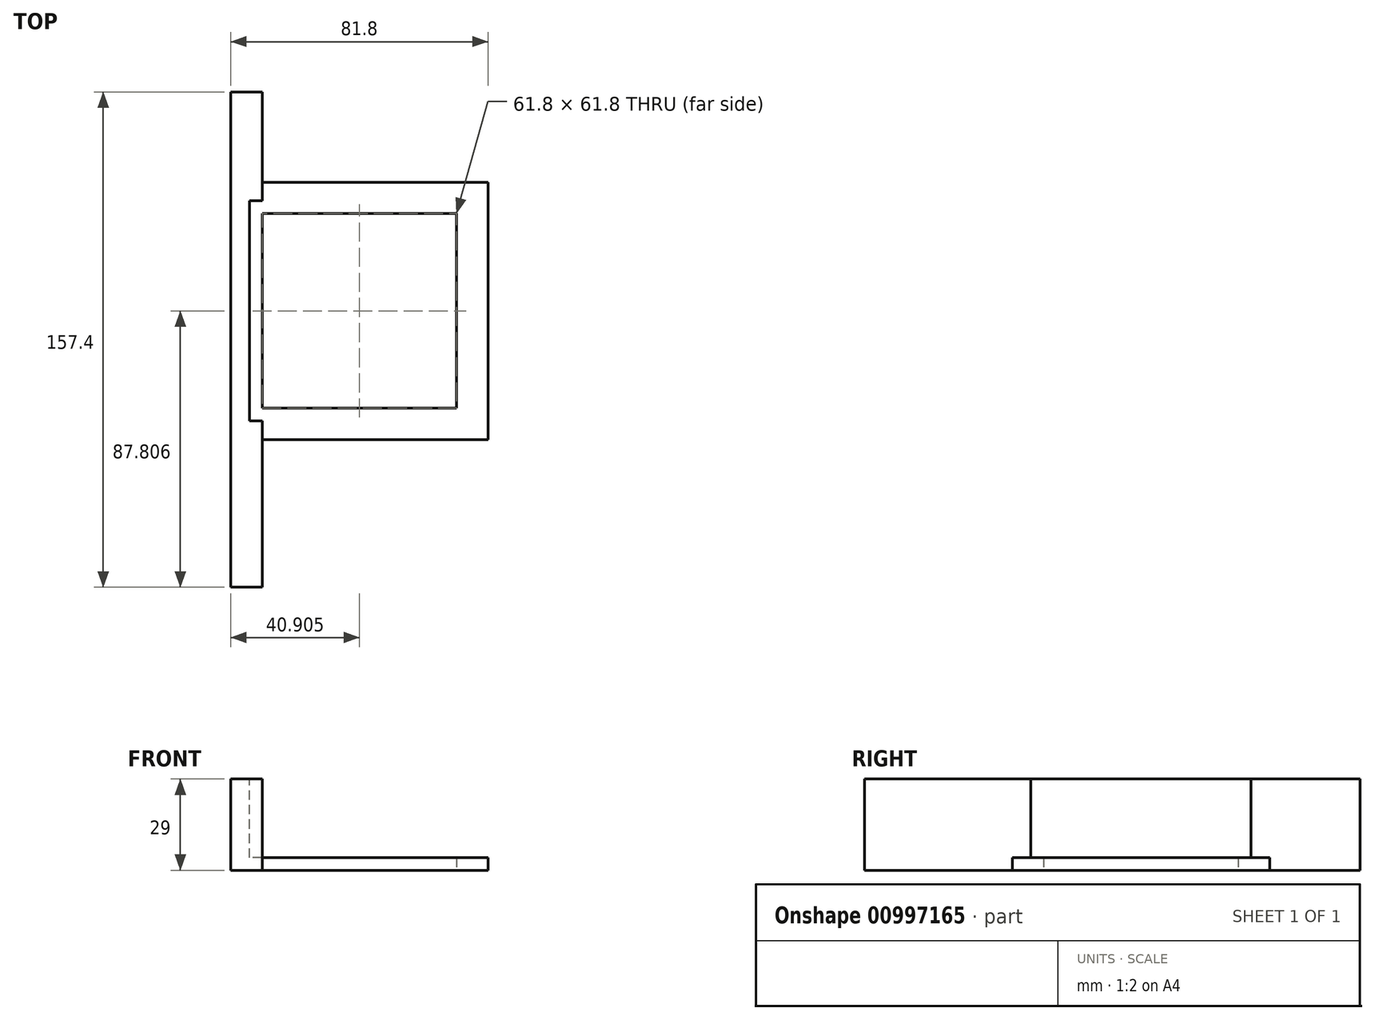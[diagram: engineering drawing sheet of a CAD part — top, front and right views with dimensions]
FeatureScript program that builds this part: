
annotation { "Feature Type Name" : "Feature", "Feature Type Description" : "" }
export const myFeature = defineFeature(function(context is Context, id is Id, definition is map)
    precondition{}
    {
        {
            var Q0;
            Q0=qCreatedBy(makeId("Top.planeOp"),FACE);
            var sketch = newSketch(context, id + "F0", { "sketchPlane" : qUnion([Q0])});
            skLineSegment(sketch, "E0.bottom", {"start": v(-15.62, 8.79) * mm, "end": v(35.18, 8.79) * mm, "construction": true});
            skLineSegment(sketch, "E0.top", {"start": v(-15.62, -42.01) * mm, "end": v(35.18, -42.01) * mm, "construction": true});
            skLineSegment(sketch, "E0.left", {"start": v(-15.62, 8.79) * mm, "end": v(-15.62, -42.01) * mm, "construction": true});
            skLineSegment(sketch, "E0.right", {"start": v(35.18, 8.79) * mm, "end": v(35.18, -42.01) * mm, "construction": true});
            skLineSegment(sketch, "E1", {"start": v(-2.92, 8.79) * mm, "end": v(-2.92, -3.91) * mm, "construction": true});
            skLineSegment(sketch, "E2", {"start": v(22.48, 8.79) * mm, "end": v(22.48, -3.91) * mm, "construction": true});
            skLineSegment(sketch, "E3", {"start": v(35.18, -29.31) * mm, "end": v(22.48, -29.31) * mm, "construction": true});
            skLineSegment(sketch, "E4", {"start": v(35.18, -3.91) * mm, "end": v(22.48, -3.91) * mm, "construction": true});
            skLineSegment(sketch, "E5", {"start": v(-2.92, -3.91) * mm, "end": v(-2.92, -29.31) * mm, "construction": true});
            skLineSegment(sketch, "E6", {"start": v(-2.92, -3.91) * mm, "end": v(-15.62, -3.91) * mm, "construction": true});
            skLineSegment(sketch, "E7", {"start": v(22.48, -3.91) * mm, "end": v(-2.92, -3.91) * mm, "construction": true});
            skLineSegment(sketch, "E8", {"start": v(22.48, -3.91) * mm, "end": v(22.48, -29.31) * mm, "construction": true});
            skLineSegment(sketch, "E9", {"start": v(22.48, -29.31) * mm, "end": v(-2.92, -29.31) * mm, "construction": true});
            skLineSegment(sketch, "E10", {"start": v(22.48, -29.31) * mm, "end": v(22.48, -42.01) * mm, "construction": true});
            skLineSegment(sketch, "E11", {"start": v(-2.92, -29.31) * mm, "end": v(-2.92, -42.01) * mm, "construction": true});
            skLineSegment(sketch, "E12", {"start": v(-2.92, -29.31) * mm, "end": v(-15.62, -29.31) * mm, "construction": true});
            skLineSegment(sketch, "E13", {"start": v(-12.12, 8.79) * mm, "end": v(-12.12, 5.29) * mm, "construction": true});
            skLineSegment(sketch, "E14", {"start": v(-15.62, -38.51) * mm, "end": v(-12.12, -38.51) * mm, "construction": true});
            skLineSegment(sketch, "E15", {"start": v(31.68, -42.01) * mm, "end": v(31.68, -38.51) * mm, "construction": true});
            skLineSegment(sketch, "E16", {"start": v(35.18, 5.29) * mm, "end": v(-12.12, 5.29) * mm, "construction": true});
            skLineSegment(sketch, "E17", {"start": v(-12.12, 5.29) * mm, "end": v(-12.12, -38.51) * mm, "construction": true});
            skLineSegment(sketch, "E18", {"start": v(-12.12, 5.29) * mm, "end": v(-15.62, 5.29) * mm, "construction": true});
            skLineSegment(sketch, "E19", {"start": v(-12.12, -38.51) * mm, "end": v(-12.12, -42.01) * mm, "construction": true});
            skLineSegment(sketch, "E20", {"start": v(-12.12, -38.51) * mm, "end": v(31.68, -38.51) * mm, "construction": true});
            skLineSegment(sketch, "E21", {"start": v(31.68, -38.51) * mm, "end": v(35.18, -38.51) * mm, "construction": true});
            skLineSegment(sketch, "E22", {"start": v(31.68, -38.51) * mm, "end": v(31.68, 5.29) * mm, "construction": true});
            skLineSegment(sketch, "E23", {"start": v(31.68, 5.29) * mm, "end": v(31.68, 8.79) * mm, "construction": true});
            skLineSegment(sketch, "E24", {"start": v(31.68, 5.29) * mm, "end": v(31.68, 5.29) * mm});
            skCircle(sketch, "E25", {"center": v(-2.92, 5.29) * mm, "radius": 3 * mm, "construction": true});
            skCircle(sketch, "E26", {"center": v(22.48, 5.29) * mm, "radius": 3 * mm, "construction": true});
            skCircle(sketch, "E27", {"center": v(31.68, -3.91) * mm, "radius": 3 * mm, "construction": true});
            skCircle(sketch, "E28", {"center": v(31.68, -29.31) * mm, "radius": 3 * mm, "construction": true});
            skCircle(sketch, "E29", {"center": v(22.48, -38.51) * mm, "radius": 3 * mm, "construction": true});
            skCircle(sketch, "E30", {"center": v(-2.92, -38.51) * mm, "radius": 3 * mm, "construction": true});
            skCircle(sketch, "E31", {"center": v(-12.12, -29.31) * mm, "radius": 3 * mm, "construction": true});
            skCircle(sketch, "E32", {"center": v(-12.12, -3.91) * mm, "radius": 3 * mm, "construction": true});
            skSolve(sketch);
        }
        {
            var Q0;
            Q0=qCreatedBy(makeId("Top.planeOp"),FACE);
            var sketch = newSketch(context, id + "F1", { "sketchPlane" : qUnion([Q0])});
            skLineSegment(sketch, "E33.bottom", {"start": v(-21.12, 14.29) * mm, "end": v(40.68, 14.29) * mm});
            skLineSegment(sketch, "E33.top", {"start": v(-21.12, -47.51) * mm, "end": v(40.68, -47.51) * mm});
            skLineSegment(sketch, "E33.left", {"start": v(-21.12, 14.29) * mm, "end": v(-21.12, -47.51) * mm});
            skLineSegment(sketch, "E33.right", {"start": v(40.68, 14.29) * mm, "end": v(40.68, -47.51) * mm});
            skLineSegment(sketch, "E34.bottom", {"start": v(-31.12, 24.29) * mm, "end": v(50.68, 24.29) * mm});
            skLineSegment(sketch, "E34.top", {"start": v(-31.12, -57.51) * mm, "end": v(50.68, -57.51) * mm});
            skLineSegment(sketch, "E34.left", {"start": v(-31.12, 24.29) * mm, "end": v(-31.12, -57.51) * mm});
            skLineSegment(sketch, "E34.right", {"start": v(50.68, 24.29) * mm, "end": v(50.68, -57.51) * mm});
            skLineSegment(sketch, "E35.bottom", {"start": v(-31.12, -57.51) * mm, "end": v(-21.12, -57.51) * mm});
            skLineSegment(sketch, "E35.top", {"start": v(-31.12, -104.42) * mm, "end": v(-21.12, -104.42) * mm});
            skLineSegment(sketch, "E35.left", {"start": v(-31.12, -57.51) * mm, "end": v(-31.12, -104.42) * mm});
            skLineSegment(sketch, "E35.right", {"start": v(-21.12, -57.51) * mm, "end": v(-21.12, -104.42) * mm});
            skSolve(sketch);
        }
        {
            var Q0;
            Q0 = qSketchRegion(id + "F1", true);
            extrude(context, id + "F2", {"entities" : qUnion([Q0]), "depth" : 4 * mm, "offsetDistance" : 25 * mm});
        }
        {
            var Q0;
            Q0=makeQuery(id+"F2.opExtrude","CAP_FACE",FACE,{"disambiguationData":[OSD([sQuery(id+"F1.wireOp",EDGE,"E33.bottom"),sQuery(id+"F1.wireOp",EDGE,"E33.top"),sQuery(id+"F1.wireOp",EDGE,"E33.left"),sQuery(id+"F1.wireOp",EDGE,"E33.right"),sQuery(id+"F1.wireOp",EDGE,"E34.bottom"),sQuery(id+"F1.wireOp",EDGE,"E34.top"),sQuery(id+"F1.wireOp",EDGE,"E34.left"),sQuery(id+"F1.wireOp",EDGE,"E34.right"),sQuery(id+"F1.wireOp",EDGE,"E35.top"),sQuery(id+"F1.wireOp",EDGE,"E35.left"),sQuery(id+"F1.wireOp",EDGE,"E35.right")])],"isStart":false});
            var sketch = newSketch(context, id + "F3", { "sketchPlane" : qUnion([Q0])});
            skLineSegment(sketch, "E36.bottom", {"start": v(-21.12, -104.42) * mm, "end": v(-31.12, -104.42) * mm});
            skLineSegment(sketch, "E36.top", {"start": v(-21.12, -56.37) * mm, "end": v(-31.12, -56.37) * mm});
            skLineSegment(sketch, "E36.left", {"start": v(-21.12, -104.42) * mm, "end": v(-21.12, -56.37) * mm});
            skLineSegment(sketch, "E36.right", {"start": v(-31.12, -104.42) * mm, "end": v(-31.12, -56.37) * mm});
            skSolve(sketch);
        }
        {
            var Q0;
            Q0 = qSketchRegion(id + "F3", true);
            extrude(context, id + "F4", {"entities" : qUnion([Q0]), "operationType" : NewBodyOperationType.ADD, "depth" : 25 * mm, "offsetDistance" : 25 * mm});
        }
        {
            var Q0;
            Q0=makeQuery(id+"F4.boolean.opBoolean","MERGE",FACE,{"derivedFrom":[makeQuery(id+"F2.opExtrude","SWEPT_FACE",FACE,{"disambiguationData":[OSD([sQuery(id+"F1.wireOp",EDGE,"E35.top")])]}),makeQuery(id+"F4.opExtrude","SWEPT_FACE",FACE,{"disambiguationData":[OSD([sQuery(id+"F3.wireOp",EDGE,"E36.bottom")])]})]});
            extrude(context, id + "F5", {"entities" : qUnion([Q0]), "operationType" : NewBodyOperationType.ADD, "oppositeDirection" : true, "depth" : 157.4 * mm, "offsetDistance" : 25 * mm});
        }
        {
            var Q0;
            {var subQ0=sQuery(id+"F3.wireOp",EDGE,"E36.bottom");Q0=makeQuery(id+"F5.boolean.opBoolean","MERGE",FACE,{"derivedFrom":[makeQuery(id+"F4.opExtrude","CAP_FACE",FACE,{"disambiguationData":[OSD([subQ0,sQuery(id+"F3.wireOp",EDGE,"E36.top"),sQuery(id+"F3.wireOp",EDGE,"E36.left"),sQuery(id+"F3.wireOp",EDGE,"E36.right")])],"isStart":false}),makeQuery(id+"F5.opExtrude","SWEPT_FACE",FACE,{"disambiguationData":[OSD([subQ0])]})]});}
            var sketch = newSketch(context, id + "F6", { "sketchPlane" : qUnion([Q0])});
            skPoint(sketch, "E37.0", {"position": v(-21.12, 14.29) * mm});
            skPoint(sketch, "E38.0", {"position": v(-21.12, -47.51) * mm});
            skLineSegment(sketch, "E39.bottom", {"start": v(-21.12, 14.29) * mm, "end": v(-25.2, 14.29) * mm});
            skLineSegment(sketch, "E39.top", {"start": v(-21.12, -47.51) * mm, "end": v(-25.2, -47.51) * mm});
            skLineSegment(sketch, "E39.left", {"start": v(-21.12, 14.29) * mm, "end": v(-21.12, -47.51) * mm});
            skLineSegment(sketch, "E39.right", {"start": v(-25.2, 14.29) * mm, "end": v(-25.2, -47.51) * mm});
            skLineSegment(sketch, "E40.top", {"start": v(-21.12, -51.6) * mm, "end": v(-25.2, -51.6) * mm});
            skLineSegment(sketch, "E40.left", {"start": v(-21.12, -47.51) * mm, "end": v(-21.12, -51.6) * mm});
            skLineSegment(sketch, "E40.right", {"start": v(-25.2, -47.51) * mm, "end": v(-25.2, -51.6) * mm});
            skLineSegment(sketch, "E41.top", {"start": v(-21.12, 18.36) * mm, "end": v(-25.2, 18.36) * mm});
            skLineSegment(sketch, "E41.left", {"start": v(-21.12, 14.29) * mm, "end": v(-21.12, 18.36) * mm});
            skLineSegment(sketch, "E41.right", {"start": v(-25.2, 14.29) * mm, "end": v(-25.2, 18.36) * mm});
            skSolve(sketch);
        }
        {
            var Q0;
            Q0 = qSketchRegion(id + "F6", true);
            extrude(context, id + "F7", {"entities" : qUnion([Q0]), "operationType" : NewBodyOperationType.REMOVE, "oppositeDirection" : true, "depth" : 25 * mm, "offsetDistance" : 25 * mm});
        }
    });
